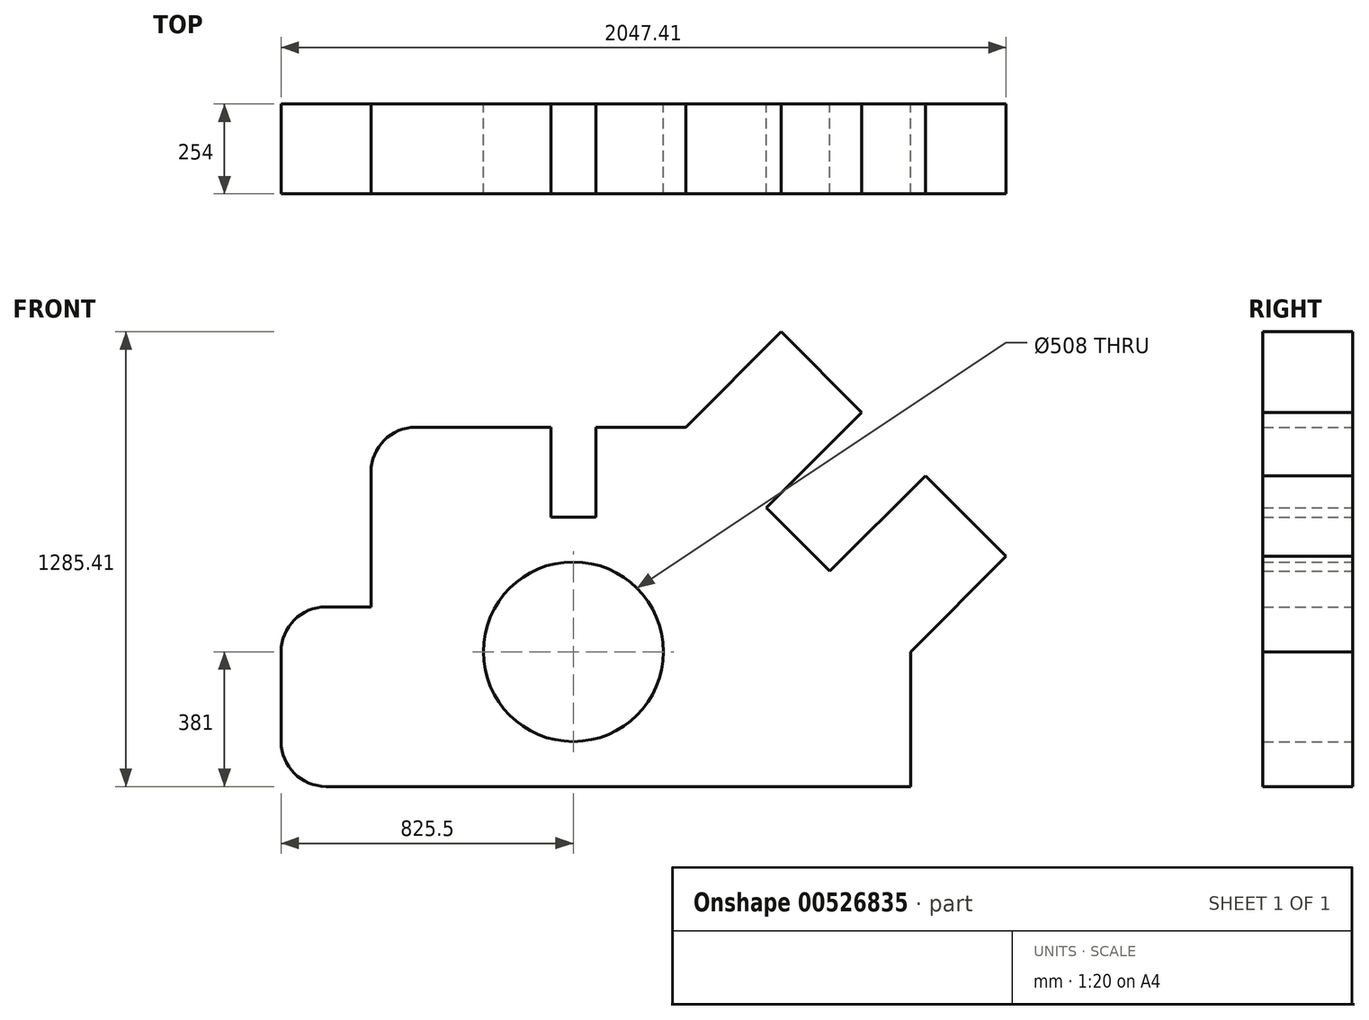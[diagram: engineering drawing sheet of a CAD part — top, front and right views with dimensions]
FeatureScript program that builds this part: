
annotation { "Feature Type Name" : "Feature", "Feature Type Description" : "" }
export const myFeature = defineFeature(function(context is Context, id is Id, definition is map)
    precondition{}
    {
        {
            var Q0;
            Q0=qCreatedBy(makeId("Front.planeOp"),FACE);
            var sketch = newSketch(context, id + "F0", { "sketchPlane" : qUnion([Q0])});
            skLineSegment(sketch, "E0", {"start": v(127, 0) * mm, "end": v(1778, 0) * mm});
            skLineSegment(sketch, "E1", {"start": v(0, 127) * mm, "end": v(0, 381) * mm});
            skLineSegment(sketch, "E2", {"start": v(1778, 0) * mm, "end": v(1778, 381) * mm});
            skPoint(sketch, "E3.visualSharp", {"position": v(0, 0) * mm});
            skArc(sketch, "E3.filletArc", {"start": v(0, 127) * mm, "mid": v(37.2, 37.2) * mm, "end": v(127, 0) * mm});
            skLineSegment(sketch, "E4", {"start": v(1778, 381) * mm, "end": v(2047.4, 650.4) * mm});
            skCircle(sketch, "E5", {"center": v(825.5, 381) * mm, "radius": 254 * mm});
            skLineSegment(sketch, "E6", {"start": v(127, 508) * mm, "end": v(254, 508) * mm});
            skPoint(sketch, "E7.visualSharp", {"position": v(0, 508) * mm});
            skArc(sketch, "E7.filletArc", {"start": v(127, 508) * mm, "mid": v(37.2, 470.8) * mm, "end": v(0, 381) * mm});
            skLineSegment(sketch, "E8", {"start": v(254, 508) * mm, "end": v(254, 889) * mm});
            skLineSegment(sketch, "E9", {"start": v(381, 1016) * mm, "end": v(762, 1016) * mm});
            skLineSegment(sketch, "E10", {"start": v(762, 1016) * mm, "end": v(762, 762) * mm});
            skLineSegment(sketch, "E11", {"start": v(762, 762) * mm, "end": v(889, 762) * mm});
            skLineSegment(sketch, "E12", {"start": v(889, 762) * mm, "end": v(889, 1016) * mm});
            skLineSegment(sketch, "E13", {"start": v(889, 1016) * mm, "end": v(1143, 1016) * mm});
            skPoint(sketch, "E14.visualSharp", {"position": v(254, 1016) * mm});
            skArc(sketch, "E14.filletArc", {"start": v(381, 1016) * mm, "mid": v(291.2, 978.8) * mm, "end": v(254, 889) * mm});
            skLineSegment(sketch, "E15", {"start": v(2047.4, 650.4) * mm, "end": v(1819.71, 878.1) * mm});
            skLineSegment(sketch, "E16", {"start": v(1819.71, 878.1) * mm, "end": v(1550.3, 608.7) * mm});
            skLineSegment(sketch, "E17", {"start": v(1550.3, 608.7) * mm, "end": v(1370.7, 788.3) * mm});
            skLineSegment(sketch, "E18", {"start": v(1370.7, 788.3) * mm, "end": v(1640.1, 1057.71) * mm});
            skLineSegment(sketch, "E19", {"start": v(1143, 1016) * mm, "end": v(1412.4, 1285.4) * mm});
            skLineSegment(sketch, "E20", {"start": v(1412.4, 1285.4) * mm, "end": v(1640.1, 1057.71) * mm});
            skSolve(sketch);
        }
        {
            var Q0;
            Q0=makeQuery(id+"F0.imprint","IMPRINT",FACE,{"disambiguationData":[TD([[makeQuery(id+"F0.imprint","IMPRINT",EDGE,{"derivedFrom":sQuery(id+"F0.wireOp",EDGE,"E0")}),1.0]])]});
            extrude(context, id + "F1", {"entities" : qUnion([Q0]), "depth" : 254 * mm, "offsetDistance" : 25.4 * mm});
        }
    });
